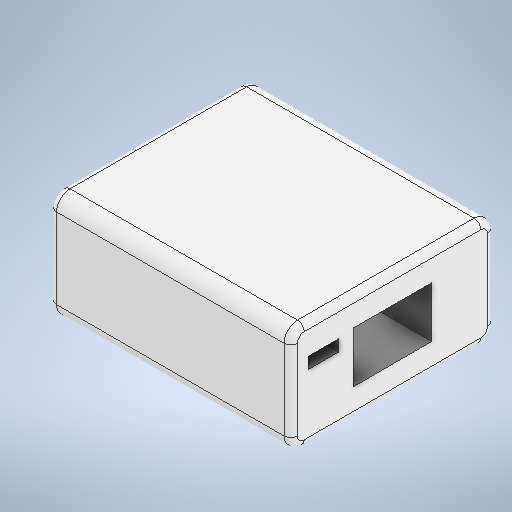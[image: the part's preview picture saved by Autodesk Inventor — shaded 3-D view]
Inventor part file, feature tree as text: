
AUTODESK INVENTOR PART (.ipt)
format: ipt  version: 2025 (Build 290162000, 162)  size: 270,848 bytes
history: native  units: in
note: dims shown in document units (in); Inventor stores cm internally (conversion verified against a paired STEP export)
features: extrude x3, sketch x3, fillet x2, projected_geometry x2, chamfer x1
ambient origin geometry x8: Origin, YZ Plane, XZ Plane, XY Plane, X Axis, Y Axis, Z Axis, Center Point
bodies: Solid1 (feature_tree)
feature tree (11):
  extrude  "Extrusion1"  Depth=1.9in
  extrude  "Extrusion2"  Depth=0.5in TaperAngle=0.0deg
  extrude  "Extrusion3"  Depth=0.3in TaperAngle=0.0deg
  chamfer  "Chamfer1"  Distance=0.3in Angle=45.0deg
  fillet  "Fillet1"  Radius=0.125in
  fillet  "Fillet2"  Radius=0.0625in
  sketch  "Sketch1"  dims[d0=2.25in d1=1.9in]
  sketch  "Sketch2"  dims[d2=1.0in d3=0.0in d4=0.5in d5=0.0in]
  projected_geometry  "Projected Loop1"
  sketch  "Sketch3"  dims[d6=0.2in d7=0.3in d8=0.0in d9=0.01in d10=0.3in d11=45.0deg d12=0.125in d13=0.0625in]
  projected_geometry  "Projected Loop2"
